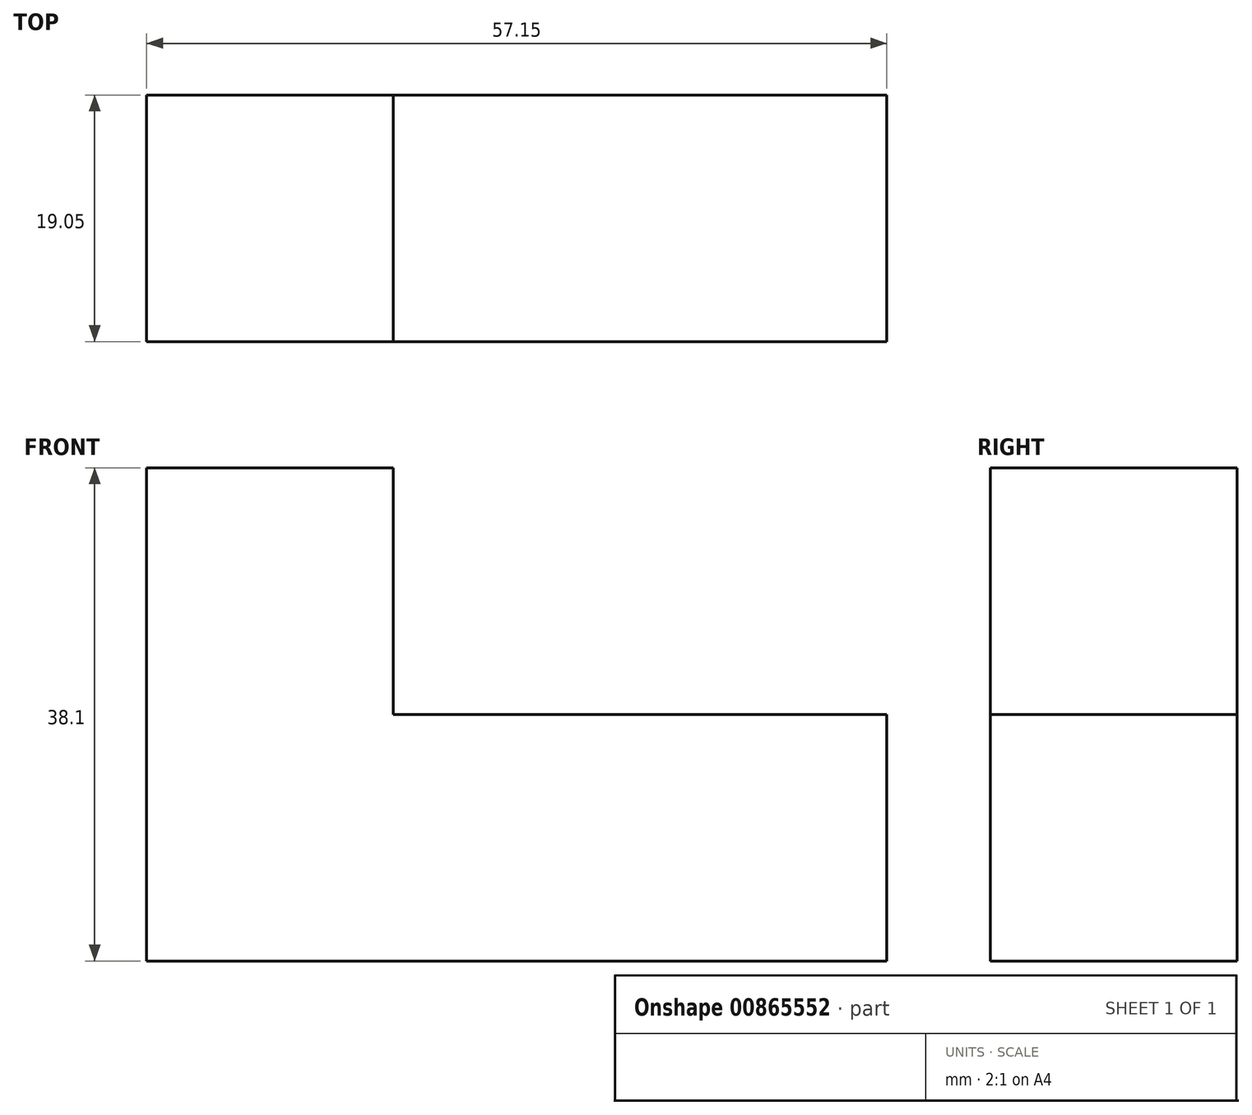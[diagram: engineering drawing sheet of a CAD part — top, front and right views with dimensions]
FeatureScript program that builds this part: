
annotation { "Feature Type Name" : "Feature", "Feature Type Description" : "" }
export const myFeature = defineFeature(function(context is Context, id is Id, definition is map)
    precondition{}
    {
        {
            var Q0;
            Q0=qCreatedBy(makeId("Front.planeOp"),FACE);
            var sketch = newSketch(context, id + "F0", { "sketchPlane" : qUnion([Q0])});
            skLineSegment(sketch, "E0", {"start": v(0, 0) * mm, "end": v(57.15, 0) * mm});
            skLineSegment(sketch, "E1", {"start": v(57.15, 0) * mm, "end": v(57.15, 19.05) * mm});
            skLineSegment(sketch, "E2", {"start": v(57.15, 19.05) * mm, "end": v(19.05, 19.05) * mm});
            skLineSegment(sketch, "E3", {"start": v(19.05, 19.05) * mm, "end": v(19.05, 38.1) * mm});
            skLineSegment(sketch, "E4", {"start": v(19.05, 38.1) * mm, "end": v(0, 38.1) * mm});
            skLineSegment(sketch, "E5", {"start": v(0, 38.1) * mm, "end": v(0, 0) * mm});
            skSolve(sketch);
        }
        {
            var Q0;
            Q0=makeQuery(id+"F0.imprint","IMPRINT",FACE,{"disambiguationData":[TD([[makeQuery(id+"F0.imprint","IMPRINT",EDGE,{"derivedFrom":sQuery(id+"F0.wireOp",EDGE,"E0")}),1.0]])]});
            extrude(context, id + "F1", {"entities" : qUnion([Q0]), "depth" : 19.05 * mm, "offsetDistance" : 25.4 * mm});
        }
    });
